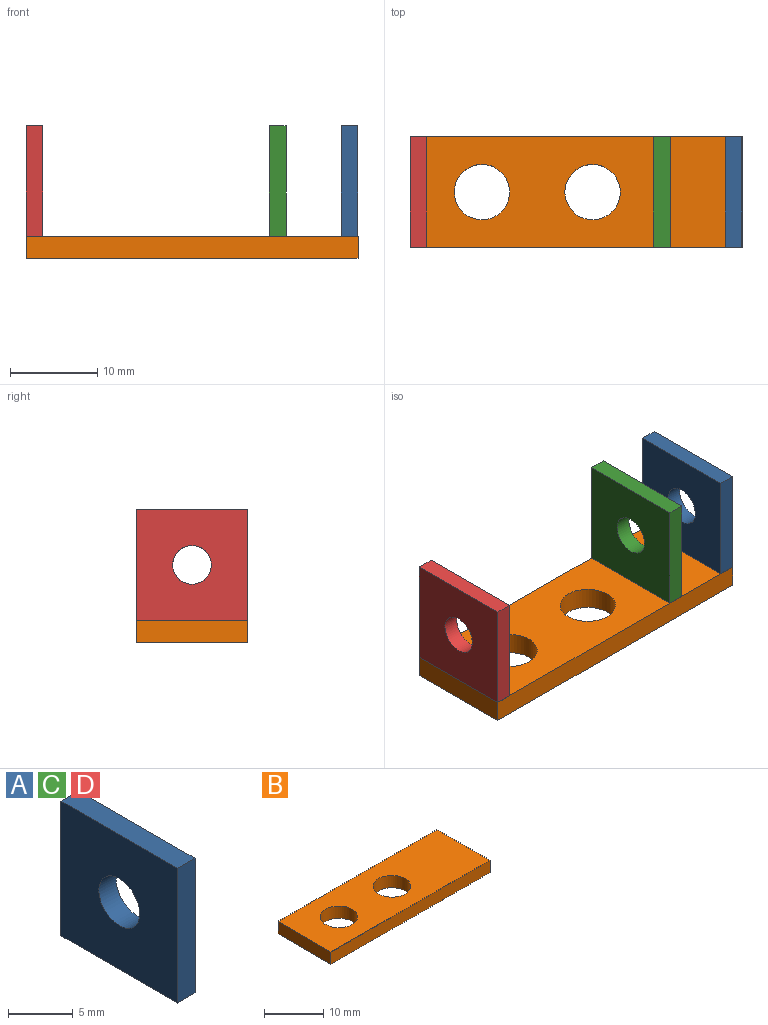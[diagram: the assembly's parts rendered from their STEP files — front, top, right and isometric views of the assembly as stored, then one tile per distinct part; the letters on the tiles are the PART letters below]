
ASSEMBLY  parts=4 mates=9
PART A: 7 faces, bbox 1.9x12.7x12.7 mm
  f0: plane 12.7x1.91mm, normal (0,0,1), area 24.2mm2, adj f1,f3,f4,f5
  f1: plane 12.7x1.91mm, normal (0,-1,0), area 24.2mm2, adj f0,f2,f4,f5
  f2: plane 12.7x1.91mm, normal (0,0,-1), area 24.2mm2, adj f1,f3,f4,f5
  f3: plane 12.7x1.91mm, normal (0,1,0), area 24.2mm2, adj f0,f2,f4,f5
  f4: plane 12.7x12.7mm, normal (1,0,0), area 145.8mm2, adj f0,f1,f2,f3,f6
  f5: plane 12.7x12.7mm, normal (-1,0,0), area 145.8mm2, adj f0,f1,f2,f3,f6
  f6: cylinder r=2.22mm len=4.45mm, axis (1,0,0), area 26.6mm2, adj f4,f5
PART B: 8 faces, bbox 38.1x12.7x2.5 mm
  f0: plane 38.1x2.54mm, normal (0,-1,0), area 96.8mm2, adj f1,f3,f4,f5
  f1: plane 12.7x2.54mm, normal (1,0,0), area 32.3mm2, adj f0,f2,f4,f5
  f2: plane 38.1x2.54mm, normal (0,1,0), area 96.8mm2, adj f1,f3,f4,f5
  f3: plane 12.7x2.54mm, normal (-1,0,0), area 32.3mm2, adj f0,f2,f4,f5
  f4: plane 38.1x12.7mm, normal (0,0,1), area 420.5mm2, adj f0,f1,f2,f3,f6,f7
  f5: plane 38.1x12.7mm, normal (0,0,-1), area 420.5mm2, adj f0,f1,f2,f3,f6,f7
  f6: cylinder r=3.17mm len=6.35mm, axis (0,0,1), area 50.7mm2, adj f4,f5
  f7: cylinder r=3.17mm len=6.35mm, axis (0,0,1), area 50.7mm2, adj f4,f5
PART C: same geometry as A
PART D: same geometry as A
PLACE A t=(46.29,-2.31,-4.79)mm
PLACE B t=(-2.95,-0.32,-1.36)mm
PLACE C t=(38.04,-2.31,-4.79)mm
PLACE D rot(axis=(1,0,0),180deg) t=(10.1,1.66,19.85)mm
MATE planar C.f6 <-> A.f6  axis (1,0,0) through (7.84,-0.32,7.53)mm
MATE planar A.f2 <-> B.f4  axis (0,0,-1) through (15.15,-0.32,1.18)mm
MATE planar A.f3 <-> B.f2  axis (0,1,0) through (15.15,6.03,7.53)mm
MATE planar D.f6 <-> B.f3  axis (-1,0,0) through (-22,-0.32,7.53)mm
MATE planar A.f6 <-> B.f1  axis (1,0,0) through (16.1,-0.32,7.53)mm
MATE cylindrical C.f6 <-> D.f6  axis (1,0,0) through (6.89,-0.32,7.53)mm
MATE cylindrical A.f6 <-> D.f6  axis (1,0,0) through (16.1,-0.32,7.53)mm
MATE planar C.f2 <-> B.f4  axis (0,0,-1) through (6.89,-0.32,1.18)mm
MATE planar D.f0 <-> B.f4  axis (0,0,-1) through (-21.05,-0.32,1.18)mm
